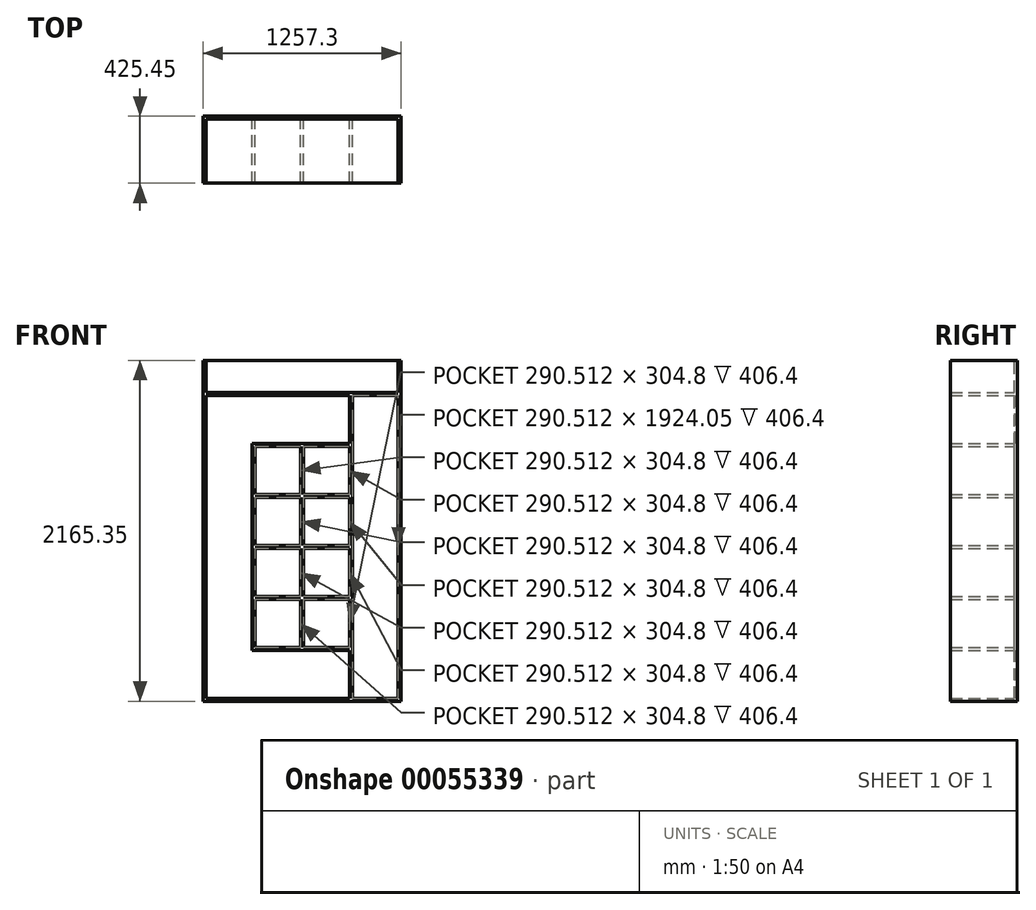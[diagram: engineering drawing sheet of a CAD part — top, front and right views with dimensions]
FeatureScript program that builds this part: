
annotation { "Feature Type Name" : "Feature", "Feature Type Description" : "" }
export const myFeature = defineFeature(function(context is Context, id is Id, definition is map)
    precondition{}
    {
        {
            var Q0;
            Q0=qCreatedBy(makeId("Front.planeOp"),FACE);
            var sketch = newSketch(context, id + "F0", { "sketchPlane" : qUnion([Q0])});
            skLineSegment(sketch, "E0.bottom", {"start": v(-913.34, 1359.41) * mm, "end": v(343.96, 1359.41) * mm});
            skLineSegment(sketch, "E0.top", {"start": v(-913.34, -805.94) * mm, "end": v(343.96, -805.94) * mm});
            skLineSegment(sketch, "E0.left", {"start": v(-913.34, 1359.41) * mm, "end": v(-913.34, -805.94) * mm});
            skLineSegment(sketch, "E0.right", {"start": v(343.96, 1359.41) * mm, "end": v(343.96, -805.94) * mm});
            skSolve(sketch);
        }
        {
            var Q0;
            Q0=makeQuery(id+"F0.imprint","IMPRINT",FACE,{"disambiguationData":[TD([[makeQuery(id+"F0.imprint","IMPRINT",EDGE,{"derivedFrom":sQuery(id+"F0.wireOp",EDGE,"E0.bottom")}),-1.0]])]});
            extrude(context, id + "F1", {"entities" : qUnion([Q0]), "depth" : 19.05 * mm});
        }
        {
            var Q0;
            Q0=makeQuery(id+"F1.opExtrude","CAP_FACE",FACE,{"disambiguationData":[OSD([sQuery(id+"F0.wireOp",EDGE,"E0.bottom"),sQuery(id+"F0.wireOp",EDGE,"E0.top"),sQuery(id+"F0.wireOp",EDGE,"E0.left"),sQuery(id+"F0.wireOp",EDGE,"E0.right")])],"isStart":false});
            var sketch = newSketch(context, id + "F2", { "sketchPlane" : qUnion([Q0])});
            skLineSegment(sketch, "E1.bottom", {"start": v(-913.34, -805.94) * mm, "end": v(-894.3, -805.94) * mm});
            skLineSegment(sketch, "E1.top", {"start": v(-913.34, 1359.41) * mm, "end": v(-894.3, 1359.41) * mm});
            skLineSegment(sketch, "E1.left", {"start": v(-913.34, -805.94) * mm, "end": v(-913.34, 1359.41) * mm});
            skLineSegment(sketch, "E1.right", {"start": v(-894.3, -805.94) * mm, "end": v(-894.3, 1359.41) * mm});
            skLineSegment(sketch, "E2.bottom", {"start": v(343.96, -805.94) * mm, "end": v(324.9, -805.94) * mm});
            skLineSegment(sketch, "E2.top", {"start": v(343.96, 1359.41) * mm, "end": v(324.9, 1359.41) * mm});
            skLineSegment(sketch, "E2.left", {"start": v(343.96, -805.94) * mm, "end": v(343.96, 1359.41) * mm});
            skLineSegment(sketch, "E2.right", {"start": v(324.9, -805.94) * mm, "end": v(324.9, 1359.41) * mm});
            skLineSegment(sketch, "E3.bottom", {"start": v(-894.3, -805.94) * mm, "end": v(324.9, -805.94) * mm});
            skLineSegment(sketch, "E3.top", {"start": v(-894.3, -786.89) * mm, "end": v(324.9, -786.89) * mm});
            skLineSegment(sketch, "E3.left", {"start": v(-894.3, -805.94) * mm, "end": v(-894.3, -786.89) * mm});
            skLineSegment(sketch, "E3.right", {"start": v(324.9, -805.94) * mm, "end": v(324.9, -786.89) * mm});
            skLineSegment(sketch, "E4.bottom", {"start": v(-894.3, -482.09) * mm, "end": v(324.9, -482.09) * mm});
            skLineSegment(sketch, "E4.top", {"start": v(-894.3, -463.04) * mm, "end": v(324.9, -463.04) * mm});
            skLineSegment(sketch, "E4.left", {"start": v(-894.3, -482.09) * mm, "end": v(-894.3, -463.04) * mm});
            skLineSegment(sketch, "E4.right", {"start": v(324.9, -482.09) * mm, "end": v(324.9, -463.04) * mm});
            skLineSegment(sketch, "E5.bottom", {"start": v(-894.3, -158.24) * mm, "end": v(324.9, -158.24) * mm});
            skLineSegment(sketch, "E5.top", {"start": v(-894.3, -139.19) * mm, "end": v(324.9, -139.19) * mm});
            skLineSegment(sketch, "E5.left", {"start": v(-894.3, -158.24) * mm, "end": v(-894.3, -139.19) * mm});
            skLineSegment(sketch, "E5.right", {"start": v(324.9, -158.24) * mm, "end": v(324.9, -139.19) * mm});
            skLineSegment(sketch, "E6.bottom", {"start": v(-894.3, 165.61) * mm, "end": v(324.9, 165.61) * mm});
            skLineSegment(sketch, "E6.top", {"start": v(-894.3, 184.66) * mm, "end": v(324.9, 184.66) * mm});
            skLineSegment(sketch, "E6.left", {"start": v(-894.3, 165.61) * mm, "end": v(-894.3, 184.66) * mm});
            skLineSegment(sketch, "E6.right", {"start": v(324.9, 165.61) * mm, "end": v(324.9, 184.66) * mm});
            skLineSegment(sketch, "E7.bottom", {"start": v(-894.3, 489.46) * mm, "end": v(324.9, 489.46) * mm});
            skLineSegment(sketch, "E7.top", {"start": v(-894.3, 508.51) * mm, "end": v(324.9, 508.51) * mm});
            skLineSegment(sketch, "E7.left", {"start": v(-894.3, 489.46) * mm, "end": v(-894.3, 508.51) * mm});
            skLineSegment(sketch, "E7.right", {"start": v(324.9, 489.46) * mm, "end": v(324.9, 508.51) * mm});
            skLineSegment(sketch, "E8.bottom", {"start": v(-894.3, 813.31) * mm, "end": v(324.9, 813.31) * mm});
            skLineSegment(sketch, "E8.top", {"start": v(-894.3, 832.36) * mm, "end": v(324.9, 832.36) * mm});
            skLineSegment(sketch, "E8.left", {"start": v(-894.3, 813.31) * mm, "end": v(-894.3, 832.36) * mm});
            skLineSegment(sketch, "E8.right", {"start": v(324.9, 813.31) * mm, "end": v(324.9, 832.36) * mm});
            skLineSegment(sketch, "E9.bottom", {"start": v(-894.3, 1137.16) * mm, "end": v(324.9, 1137.16) * mm});
            skLineSegment(sketch, "E9.top", {"start": v(-894.3, 1156.21) * mm, "end": v(324.9, 1156.21) * mm});
            skLineSegment(sketch, "E9.left", {"start": v(-894.3, 1137.16) * mm, "end": v(-894.3, 1156.21) * mm});
            skLineSegment(sketch, "E9.right", {"start": v(324.9, 1137.16) * mm, "end": v(324.9, 1156.21) * mm});
            skLineSegment(sketch, "E10.bottom", {"start": v(-603.78, -786.89) * mm, "end": v(-584.73, -786.89) * mm});
            skLineSegment(sketch, "E10.top", {"start": v(-603.78, 1137.16) * mm, "end": v(-584.73, 1137.16) * mm});
            skLineSegment(sketch, "E10.left", {"start": v(-603.78, -786.89) * mm, "end": v(-603.78, 1137.16) * mm});
            skLineSegment(sketch, "E10.right", {"start": v(-584.73, -786.89) * mm, "end": v(-584.73, 1137.16) * mm});
            skLineSegment(sketch, "E11.bottom", {"start": v(-294.22, -786.89) * mm, "end": v(-275.17, -786.89) * mm});
            skLineSegment(sketch, "E11.top", {"start": v(-294.22, 1137.16) * mm, "end": v(-275.17, 1137.16) * mm});
            skLineSegment(sketch, "E11.left", {"start": v(-294.22, -786.89) * mm, "end": v(-294.22, 1137.16) * mm});
            skLineSegment(sketch, "E11.right", {"start": v(-275.17, -786.89) * mm, "end": v(-275.17, 1137.16) * mm});
            skLineSegment(sketch, "E12.bottom", {"start": v(0, -786.89) * mm, "end": v(19.05, -786.89) * mm});
            skLineSegment(sketch, "E12.top", {"start": v(0, 1137.16) * mm, "end": v(19.05, 1137.16) * mm});
            skLineSegment(sketch, "E13.bottom", {"start": v(34.4, 1137.16) * mm, "end": v(15.35, 1137.16) * mm});
            skLineSegment(sketch, "E13.top", {"start": v(34.4, -786.89) * mm, "end": v(15.35, -786.89) * mm});
            skLineSegment(sketch, "E13.left", {"start": v(34.4, 1137.16) * mm, "end": v(34.4, -786.89) * mm});
            skLineSegment(sketch, "E13.right", {"start": v(15.35, 1137.16) * mm, "end": v(15.35, -786.89) * mm});
            skSolve(sketch);
        }
        {
            var Q0;
            Q0 = qSketchRegion(id + "F2", true);
            var Q1;
            {var subQ0=sQuery(id+"F2.wireOp",EDGE,"E10.left");var subQ1=sQuery(id+"F2.wireOp",EDGE,"E7.top");var subQ2=makeQuery(id+"F2.imprint","INTERSECT",VERTEX,{"derivedFrom":[subQ1,subQ0]});Q1=makeQuery(id+"F2.imprint","IMPRINT",FACE,{"disambiguationData":[TD([[makeQuery(id+"F2.imprint","IMPRINT",EDGE,{"disambiguationData":[TD([[subQ2,-1.0]])],"derivedFrom":subQ1}),1.0]])]});}
            var Q2;
            {var subQ5=sQuery(id+"F2.wireOp",EDGE,"E10.top");Q2=makeQuery(id+"F2.imprint","IMPRINT",FACE,{"disambiguationData":[TD([[makeQuery(id+"F2.imprint","IMPRINT",EDGE,{"derivedFrom":subQ5}),-1.0]])]});}
            var Q3;
            {var subQ0=sQuery(id+"F2.wireOp",EDGE,"E8.left");Q3=makeQuery(id+"F2.imprint","IMPRINT",FACE,{"disambiguationData":[TD([[makeQuery(id+"F2.imprint","IMPRINT",EDGE,{"derivedFrom":subQ0}),-1.0]])]});}
            var Q4;
            {var subQ0=sQuery(id+"F2.wireOp",EDGE,"E10.right");var subQ1=sQuery(id+"F2.wireOp",EDGE,"E8.bottom");var subQ2=makeQuery(id+"F2.imprint","INTERSECT",VERTEX,{"derivedFrom":[subQ1,subQ0]});Q4=makeQuery(id+"F2.imprint","IMPRINT",FACE,{"disambiguationData":[TD([[makeQuery(id+"F2.imprint","IMPRINT",EDGE,{"disambiguationData":[TD([[subQ2,-1.0]])],"derivedFrom":subQ1}),1.0]])]});}
            var Q5;
            {var subQ0=sQuery(id+"F2.wireOp",EDGE,"E10.left");var subQ1=sQuery(id+"F2.wireOp",EDGE,"E8.bottom");var subQ2=makeQuery(id+"F2.imprint","INTERSECT",VERTEX,{"derivedFrom":[subQ1,subQ0]});Q5=makeQuery(id+"F2.imprint","IMPRINT",FACE,{"disambiguationData":[TD([[makeQuery(id+"F2.imprint","IMPRINT",EDGE,{"disambiguationData":[TD([[subQ2,-1.0]])],"derivedFrom":subQ1}),1.0]])]});}
            var Q6;
            {var subQ0=sQuery(id+"F2.wireOp",EDGE,"E11.left");var subQ1=sQuery(id+"F2.wireOp",EDGE,"E8.bottom");var subQ2=makeQuery(id+"F2.imprint","INTERSECT",VERTEX,{"derivedFrom":[subQ1,subQ0]});Q6=makeQuery(id+"F2.imprint","IMPRINT",FACE,{"disambiguationData":[TD([[makeQuery(id+"F2.imprint","IMPRINT",EDGE,{"disambiguationData":[TD([[subQ2,-1.0]])],"derivedFrom":subQ1}),1.0]])]});}
            var Q7;
            {var subQ0=sQuery(id+"F2.wireOp",EDGE,"E11.right");var subQ1=sQuery(id+"F2.wireOp",EDGE,"E8.bottom");var subQ2=makeQuery(id+"F2.imprint","INTERSECT",VERTEX,{"derivedFrom":[subQ1,subQ0]});Q7=makeQuery(id+"F2.imprint","IMPRINT",FACE,{"disambiguationData":[TD([[makeQuery(id+"F2.imprint","IMPRINT",EDGE,{"disambiguationData":[TD([[subQ2,-1.0]])],"derivedFrom":subQ1}),1.0]])]});}
            var Q8;
            {var subQ0=sQuery(id+"F2.wireOp",EDGE,"E13.right");var subQ1=sQuery(id+"F2.wireOp",EDGE,"E8.bottom");var subQ2=makeQuery(id+"F2.imprint","INTERSECT",VERTEX,{"derivedFrom":[subQ1,subQ0]});Q8=makeQuery(id+"F2.imprint","IMPRINT",FACE,{"disambiguationData":[TD([[makeQuery(id+"F2.imprint","IMPRINT",EDGE,{"disambiguationData":[TD([[subQ2,-1.0]])],"derivedFrom":subQ1}),1.0]])]});}
            var Q9;
            {var subQ0=sQuery(id+"F2.wireOp",EDGE,"E8.right");Q9=makeQuery(id+"F2.imprint","IMPRINT",FACE,{"disambiguationData":[TD([[makeQuery(id+"F2.imprint","IMPRINT",EDGE,{"derivedFrom":subQ0}),1.0]])]});}
            var Q10;
            {var subQ3=sQuery(id+"F2.wireOp",EDGE,"E8.top");var subQ5=sQuery(id+"F2.wireOp",EDGE,"E13.right");var subQ8=makeQuery(id+"F2.imprint","INTERSECT",VERTEX,{"derivedFrom":[subQ3,subQ5]});Q10=makeQuery(id+"F2.imprint","IMPRINT",FACE,{"disambiguationData":[TD([[makeQuery(id+"F2.imprint","IMPRINT",EDGE,{"disambiguationData":[TD([[subQ8,-1.0]])],"derivedFrom":subQ3}),1.0]])]});}
            var Q11;
            {var subQ5=sQuery(id+"F2.wireOp",EDGE,"E11.top");Q11=makeQuery(id+"F2.imprint","IMPRINT",FACE,{"disambiguationData":[TD([[makeQuery(id+"F2.imprint","IMPRINT",EDGE,{"derivedFrom":subQ5}),-1.0]])]});}
            var Q12;
            {var subQ0=sQuery(id+"F2.wireOp",EDGE,"E11.left");var subQ1=sQuery(id+"F2.wireOp",EDGE,"E7.top");var subQ2=makeQuery(id+"F2.imprint","INTERSECT",VERTEX,{"derivedFrom":[subQ1,subQ0]});Q12=makeQuery(id+"F2.imprint","IMPRINT",FACE,{"disambiguationData":[TD([[makeQuery(id+"F2.imprint","IMPRINT",EDGE,{"disambiguationData":[TD([[subQ2,-1.0]])],"derivedFrom":subQ1}),1.0]])]});}
            var Q13;
            {var subQ0=sQuery(id+"F2.wireOp",EDGE,"E13.right");var subQ1=sQuery(id+"F2.wireOp",EDGE,"E7.top");var subQ2=makeQuery(id+"F2.imprint","INTERSECT",VERTEX,{"derivedFrom":[subQ1,subQ0]});Q13=makeQuery(id+"F2.imprint","IMPRINT",FACE,{"disambiguationData":[TD([[makeQuery(id+"F2.imprint","IMPRINT",EDGE,{"disambiguationData":[TD([[subQ2,-1.0]])],"derivedFrom":subQ1}),1.0]])]});}
            var Q14;
            {var subQ0=sQuery(id+"F2.wireOp",EDGE,"E7.left");Q14=makeQuery(id+"F2.imprint","IMPRINT",FACE,{"disambiguationData":[TD([[makeQuery(id+"F2.imprint","IMPRINT",EDGE,{"derivedFrom":subQ0}),-1.0]])]});}
            var Q15;
            {var subQ0=sQuery(id+"F2.wireOp",EDGE,"E10.left");var subQ1=sQuery(id+"F2.wireOp",EDGE,"E7.bottom");var subQ2=makeQuery(id+"F2.imprint","INTERSECT",VERTEX,{"derivedFrom":[subQ1,subQ0]});Q15=makeQuery(id+"F2.imprint","IMPRINT",FACE,{"disambiguationData":[TD([[makeQuery(id+"F2.imprint","IMPRINT",EDGE,{"disambiguationData":[TD([[subQ2,-1.0]])],"derivedFrom":subQ1}),1.0]])]});}
            var Q16;
            {var subQ0=sQuery(id+"F2.wireOp",EDGE,"E10.right");var subQ1=sQuery(id+"F2.wireOp",EDGE,"E7.bottom");var subQ2=makeQuery(id+"F2.imprint","INTERSECT",VERTEX,{"derivedFrom":[subQ1,subQ0]});Q16=makeQuery(id+"F2.imprint","IMPRINT",FACE,{"disambiguationData":[TD([[makeQuery(id+"F2.imprint","IMPRINT",EDGE,{"disambiguationData":[TD([[subQ2,-1.0]])],"derivedFrom":subQ1}),1.0]])]});}
            var Q17;
            {var subQ0=sQuery(id+"F2.wireOp",EDGE,"E11.left");var subQ1=sQuery(id+"F2.wireOp",EDGE,"E7.bottom");var subQ2=makeQuery(id+"F2.imprint","INTERSECT",VERTEX,{"derivedFrom":[subQ1,subQ0]});Q17=makeQuery(id+"F2.imprint","IMPRINT",FACE,{"disambiguationData":[TD([[makeQuery(id+"F2.imprint","IMPRINT",EDGE,{"disambiguationData":[TD([[subQ2,-1.0]])],"derivedFrom":subQ1}),1.0]])]});}
            var Q18;
            {var subQ0=sQuery(id+"F2.wireOp",EDGE,"E11.right");var subQ1=sQuery(id+"F2.wireOp",EDGE,"E7.bottom");var subQ2=makeQuery(id+"F2.imprint","INTERSECT",VERTEX,{"derivedFrom":[subQ1,subQ0]});Q18=makeQuery(id+"F2.imprint","IMPRINT",FACE,{"disambiguationData":[TD([[makeQuery(id+"F2.imprint","IMPRINT",EDGE,{"disambiguationData":[TD([[subQ2,-1.0]])],"derivedFrom":subQ1}),1.0]])]});}
            var Q19;
            {var subQ0=sQuery(id+"F2.wireOp",EDGE,"E13.right");var subQ1=sQuery(id+"F2.wireOp",EDGE,"E7.bottom");var subQ2=makeQuery(id+"F2.imprint","INTERSECT",VERTEX,{"derivedFrom":[subQ1,subQ0]});Q19=makeQuery(id+"F2.imprint","IMPRINT",FACE,{"disambiguationData":[TD([[makeQuery(id+"F2.imprint","IMPRINT",EDGE,{"disambiguationData":[TD([[subQ2,-1.0]])],"derivedFrom":subQ1}),1.0]])]});}
            var Q20;
            {var subQ0=sQuery(id+"F2.wireOp",EDGE,"E7.right");Q20=makeQuery(id+"F2.imprint","IMPRINT",FACE,{"disambiguationData":[TD([[makeQuery(id+"F2.imprint","IMPRINT",EDGE,{"derivedFrom":subQ0}),1.0]])]});}
            var Q21;
            {var subQ0=sQuery(id+"F2.wireOp",EDGE,"E6.left");Q21=makeQuery(id+"F2.imprint","IMPRINT",FACE,{"disambiguationData":[TD([[makeQuery(id+"F2.imprint","IMPRINT",EDGE,{"derivedFrom":subQ0}),-1.0]])]});}
            var Q22;
            {var subQ0=sQuery(id+"F2.wireOp",EDGE,"E10.left");var subQ1=sQuery(id+"F2.wireOp",EDGE,"E6.bottom");var subQ2=makeQuery(id+"F2.imprint","INTERSECT",VERTEX,{"derivedFrom":[subQ1,subQ0]});Q22=makeQuery(id+"F2.imprint","IMPRINT",FACE,{"disambiguationData":[TD([[makeQuery(id+"F2.imprint","IMPRINT",EDGE,{"disambiguationData":[TD([[subQ2,-1.0]])],"derivedFrom":subQ1}),1.0]])]});}
            var Q23;
            {var subQ0=sQuery(id+"F2.wireOp",EDGE,"E10.right");var subQ1=sQuery(id+"F2.wireOp",EDGE,"E6.bottom");var subQ2=makeQuery(id+"F2.imprint","INTERSECT",VERTEX,{"derivedFrom":[subQ1,subQ0]});Q23=makeQuery(id+"F2.imprint","IMPRINT",FACE,{"disambiguationData":[TD([[makeQuery(id+"F2.imprint","IMPRINT",EDGE,{"disambiguationData":[TD([[subQ2,-1.0]])],"derivedFrom":subQ1}),1.0]])]});}
            var Q24;
            {var subQ0=sQuery(id+"F2.wireOp",EDGE,"E11.left");var subQ1=sQuery(id+"F2.wireOp",EDGE,"E6.bottom");var subQ2=makeQuery(id+"F2.imprint","INTERSECT",VERTEX,{"derivedFrom":[subQ1,subQ0]});Q24=makeQuery(id+"F2.imprint","IMPRINT",FACE,{"disambiguationData":[TD([[makeQuery(id+"F2.imprint","IMPRINT",EDGE,{"disambiguationData":[TD([[subQ2,-1.0]])],"derivedFrom":subQ1}),1.0]])]});}
            var Q25;
            {var subQ0=sQuery(id+"F2.wireOp",EDGE,"E11.right");var subQ1=sQuery(id+"F2.wireOp",EDGE,"E6.bottom");var subQ2=makeQuery(id+"F2.imprint","INTERSECT",VERTEX,{"derivedFrom":[subQ1,subQ0]});Q25=makeQuery(id+"F2.imprint","IMPRINT",FACE,{"disambiguationData":[TD([[makeQuery(id+"F2.imprint","IMPRINT",EDGE,{"disambiguationData":[TD([[subQ2,-1.0]])],"derivedFrom":subQ1}),1.0]])]});}
            var Q26;
            {var subQ0=sQuery(id+"F2.wireOp",EDGE,"E13.right");var subQ1=sQuery(id+"F2.wireOp",EDGE,"E6.bottom");var subQ2=makeQuery(id+"F2.imprint","INTERSECT",VERTEX,{"derivedFrom":[subQ1,subQ0]});Q26=makeQuery(id+"F2.imprint","IMPRINT",FACE,{"disambiguationData":[TD([[makeQuery(id+"F2.imprint","IMPRINT",EDGE,{"disambiguationData":[TD([[subQ2,-1.0]])],"derivedFrom":subQ1}),1.0]])]});}
            var Q27;
            {var subQ0=sQuery(id+"F2.wireOp",EDGE,"E6.right");Q27=makeQuery(id+"F2.imprint","IMPRINT",FACE,{"disambiguationData":[TD([[makeQuery(id+"F2.imprint","IMPRINT",EDGE,{"derivedFrom":subQ0}),1.0]])]});}
            var Q28;
            {var subQ0=sQuery(id+"F2.wireOp",EDGE,"E13.right");var subQ1=sQuery(id+"F2.wireOp",EDGE,"E6.top");var subQ2=makeQuery(id+"F2.imprint","INTERSECT",VERTEX,{"derivedFrom":[subQ1,subQ0]});Q28=makeQuery(id+"F2.imprint","IMPRINT",FACE,{"disambiguationData":[TD([[makeQuery(id+"F2.imprint","IMPRINT",EDGE,{"disambiguationData":[TD([[subQ2,-1.0]])],"derivedFrom":subQ1}),1.0]])]});}
            var Q29;
            {var subQ0=sQuery(id+"F2.wireOp",EDGE,"E11.left");var subQ1=sQuery(id+"F2.wireOp",EDGE,"E6.top");var subQ2=makeQuery(id+"F2.imprint","INTERSECT",VERTEX,{"derivedFrom":[subQ1,subQ0]});Q29=makeQuery(id+"F2.imprint","IMPRINT",FACE,{"disambiguationData":[TD([[makeQuery(id+"F2.imprint","IMPRINT",EDGE,{"disambiguationData":[TD([[subQ2,-1.0]])],"derivedFrom":subQ1}),1.0]])]});}
            var Q30;
            {var subQ0=sQuery(id+"F2.wireOp",EDGE,"E10.left");var subQ1=sQuery(id+"F2.wireOp",EDGE,"E6.top");var subQ2=makeQuery(id+"F2.imprint","INTERSECT",VERTEX,{"derivedFrom":[subQ1,subQ0]});Q30=makeQuery(id+"F2.imprint","IMPRINT",FACE,{"disambiguationData":[TD([[makeQuery(id+"F2.imprint","IMPRINT",EDGE,{"disambiguationData":[TD([[subQ2,-1.0]])],"derivedFrom":subQ1}),1.0]])]});}
            var Q31;
            {var subQ0=sQuery(id+"F2.wireOp",EDGE,"E5.left");Q31=makeQuery(id+"F2.imprint","IMPRINT",FACE,{"disambiguationData":[TD([[makeQuery(id+"F2.imprint","IMPRINT",EDGE,{"derivedFrom":subQ0}),-1.0]])]});}
            var Q32;
            {var subQ0=sQuery(id+"F2.wireOp",EDGE,"E10.left");var subQ1=sQuery(id+"F2.wireOp",EDGE,"E5.bottom");var subQ2=makeQuery(id+"F2.imprint","INTERSECT",VERTEX,{"derivedFrom":[subQ1,subQ0]});Q32=makeQuery(id+"F2.imprint","IMPRINT",FACE,{"disambiguationData":[TD([[makeQuery(id+"F2.imprint","IMPRINT",EDGE,{"disambiguationData":[TD([[subQ2,-1.0]])],"derivedFrom":subQ1}),1.0]])]});}
            var Q33;
            {var subQ0=sQuery(id+"F2.wireOp",EDGE,"E10.right");var subQ1=sQuery(id+"F2.wireOp",EDGE,"E5.bottom");var subQ2=makeQuery(id+"F2.imprint","INTERSECT",VERTEX,{"derivedFrom":[subQ1,subQ0]});Q33=makeQuery(id+"F2.imprint","IMPRINT",FACE,{"disambiguationData":[TD([[makeQuery(id+"F2.imprint","IMPRINT",EDGE,{"disambiguationData":[TD([[subQ2,-1.0]])],"derivedFrom":subQ1}),1.0]])]});}
            var Q34;
            {var subQ0=sQuery(id+"F2.wireOp",EDGE,"E11.left");var subQ1=sQuery(id+"F2.wireOp",EDGE,"E5.bottom");var subQ2=makeQuery(id+"F2.imprint","INTERSECT",VERTEX,{"derivedFrom":[subQ1,subQ0]});Q34=makeQuery(id+"F2.imprint","IMPRINT",FACE,{"disambiguationData":[TD([[makeQuery(id+"F2.imprint","IMPRINT",EDGE,{"disambiguationData":[TD([[subQ2,-1.0]])],"derivedFrom":subQ1}),1.0]])]});}
            var Q35;
            {var subQ0=sQuery(id+"F2.wireOp",EDGE,"E11.right");var subQ1=sQuery(id+"F2.wireOp",EDGE,"E5.bottom");var subQ2=makeQuery(id+"F2.imprint","INTERSECT",VERTEX,{"derivedFrom":[subQ1,subQ0]});Q35=makeQuery(id+"F2.imprint","IMPRINT",FACE,{"disambiguationData":[TD([[makeQuery(id+"F2.imprint","IMPRINT",EDGE,{"disambiguationData":[TD([[subQ2,-1.0]])],"derivedFrom":subQ1}),1.0]])]});}
            var Q36;
            {var subQ0=sQuery(id+"F2.wireOp",EDGE,"E13.right");var subQ1=sQuery(id+"F2.wireOp",EDGE,"E5.bottom");var subQ2=makeQuery(id+"F2.imprint","INTERSECT",VERTEX,{"derivedFrom":[subQ1,subQ0]});Q36=makeQuery(id+"F2.imprint","IMPRINT",FACE,{"disambiguationData":[TD([[makeQuery(id+"F2.imprint","IMPRINT",EDGE,{"disambiguationData":[TD([[subQ2,-1.0]])],"derivedFrom":subQ1}),1.0]])]});}
            var Q37;
            {var subQ0=sQuery(id+"F2.wireOp",EDGE,"E5.right");Q37=makeQuery(id+"F2.imprint","IMPRINT",FACE,{"disambiguationData":[TD([[makeQuery(id+"F2.imprint","IMPRINT",EDGE,{"derivedFrom":subQ0}),1.0]])]});}
            var Q38;
            {var subQ0=sQuery(id+"F2.wireOp",EDGE,"E10.left");var subQ1=sQuery(id+"F2.wireOp",EDGE,"E5.top");var subQ2=makeQuery(id+"F2.imprint","INTERSECT",VERTEX,{"derivedFrom":[subQ1,subQ0]});Q38=makeQuery(id+"F2.imprint","IMPRINT",FACE,{"disambiguationData":[TD([[makeQuery(id+"F2.imprint","IMPRINT",EDGE,{"disambiguationData":[TD([[subQ2,-1.0]])],"derivedFrom":subQ1}),1.0]])]});}
            var Q39;
            {var subQ0=sQuery(id+"F2.wireOp",EDGE,"E11.left");var subQ1=sQuery(id+"F2.wireOp",EDGE,"E5.top");var subQ2=makeQuery(id+"F2.imprint","INTERSECT",VERTEX,{"derivedFrom":[subQ1,subQ0]});Q39=makeQuery(id+"F2.imprint","IMPRINT",FACE,{"disambiguationData":[TD([[makeQuery(id+"F2.imprint","IMPRINT",EDGE,{"disambiguationData":[TD([[subQ2,-1.0]])],"derivedFrom":subQ1}),1.0]])]});}
            var Q40;
            {var subQ0=sQuery(id+"F2.wireOp",EDGE,"E13.right");var subQ1=sQuery(id+"F2.wireOp",EDGE,"E5.top");var subQ2=makeQuery(id+"F2.imprint","INTERSECT",VERTEX,{"derivedFrom":[subQ1,subQ0]});Q40=makeQuery(id+"F2.imprint","IMPRINT",FACE,{"disambiguationData":[TD([[makeQuery(id+"F2.imprint","IMPRINT",EDGE,{"disambiguationData":[TD([[subQ2,-1.0]])],"derivedFrom":subQ1}),1.0]])]});}
            var Q41;
            {var subQ0=sQuery(id+"F2.wireOp",EDGE,"E4.left");Q41=makeQuery(id+"F2.imprint","IMPRINT",FACE,{"disambiguationData":[TD([[makeQuery(id+"F2.imprint","IMPRINT",EDGE,{"derivedFrom":subQ0}),-1.0]])]});}
            var Q42;
            {var subQ0=sQuery(id+"F2.wireOp",EDGE,"E10.left");var subQ1=sQuery(id+"F2.wireOp",EDGE,"E4.bottom");var subQ2=makeQuery(id+"F2.imprint","INTERSECT",VERTEX,{"derivedFrom":[subQ1,subQ0]});Q42=makeQuery(id+"F2.imprint","IMPRINT",FACE,{"disambiguationData":[TD([[makeQuery(id+"F2.imprint","IMPRINT",EDGE,{"disambiguationData":[TD([[subQ2,-1.0]])],"derivedFrom":subQ1}),1.0]])]});}
            var Q43;
            {var subQ0=sQuery(id+"F2.wireOp",EDGE,"E10.right");var subQ1=sQuery(id+"F2.wireOp",EDGE,"E4.bottom");var subQ2=makeQuery(id+"F2.imprint","INTERSECT",VERTEX,{"derivedFrom":[subQ1,subQ0]});Q43=makeQuery(id+"F2.imprint","IMPRINT",FACE,{"disambiguationData":[TD([[makeQuery(id+"F2.imprint","IMPRINT",EDGE,{"disambiguationData":[TD([[subQ2,-1.0]])],"derivedFrom":subQ1}),1.0]])]});}
            var Q44;
            {var subQ0=sQuery(id+"F2.wireOp",EDGE,"E11.left");var subQ1=sQuery(id+"F2.wireOp",EDGE,"E4.bottom");var subQ2=makeQuery(id+"F2.imprint","INTERSECT",VERTEX,{"derivedFrom":[subQ1,subQ0]});Q44=makeQuery(id+"F2.imprint","IMPRINT",FACE,{"disambiguationData":[TD([[makeQuery(id+"F2.imprint","IMPRINT",EDGE,{"disambiguationData":[TD([[subQ2,-1.0]])],"derivedFrom":subQ1}),1.0]])]});}
            var Q45;
            {var subQ0=sQuery(id+"F2.wireOp",EDGE,"E11.right");var subQ1=sQuery(id+"F2.wireOp",EDGE,"E4.bottom");var subQ2=makeQuery(id+"F2.imprint","INTERSECT",VERTEX,{"derivedFrom":[subQ1,subQ0]});Q45=makeQuery(id+"F2.imprint","IMPRINT",FACE,{"disambiguationData":[TD([[makeQuery(id+"F2.imprint","IMPRINT",EDGE,{"disambiguationData":[TD([[subQ2,-1.0]])],"derivedFrom":subQ1}),1.0]])]});}
            var Q46;
            {var subQ0=sQuery(id+"F2.wireOp",EDGE,"E13.right");var subQ1=sQuery(id+"F2.wireOp",EDGE,"E4.bottom");var subQ2=makeQuery(id+"F2.imprint","INTERSECT",VERTEX,{"derivedFrom":[subQ1,subQ0]});Q46=makeQuery(id+"F2.imprint","IMPRINT",FACE,{"disambiguationData":[TD([[makeQuery(id+"F2.imprint","IMPRINT",EDGE,{"disambiguationData":[TD([[subQ2,-1.0]])],"derivedFrom":subQ1}),1.0]])]});}
            var Q47;
            {var subQ0=sQuery(id+"F2.wireOp",EDGE,"E4.right");Q47=makeQuery(id+"F2.imprint","IMPRINT",FACE,{"disambiguationData":[TD([[makeQuery(id+"F2.imprint","IMPRINT",EDGE,{"derivedFrom":subQ0}),1.0]])]});}
            var Q48;
            {var subQ0=sQuery(id+"F2.wireOp",EDGE,"E10.left");var subQ1=sQuery(id+"F2.wireOp",EDGE,"E4.top");var subQ2=makeQuery(id+"F2.imprint","INTERSECT",VERTEX,{"derivedFrom":[subQ1,subQ0]});Q48=makeQuery(id+"F2.imprint","IMPRINT",FACE,{"disambiguationData":[TD([[makeQuery(id+"F2.imprint","IMPRINT",EDGE,{"disambiguationData":[TD([[subQ2,-1.0]])],"derivedFrom":subQ1}),1.0]])]});}
            var Q49;
            {var subQ0=sQuery(id+"F2.wireOp",EDGE,"E11.left");var subQ1=sQuery(id+"F2.wireOp",EDGE,"E4.top");var subQ2=makeQuery(id+"F2.imprint","INTERSECT",VERTEX,{"derivedFrom":[subQ1,subQ0]});Q49=makeQuery(id+"F2.imprint","IMPRINT",FACE,{"disambiguationData":[TD([[makeQuery(id+"F2.imprint","IMPRINT",EDGE,{"disambiguationData":[TD([[subQ2,-1.0]])],"derivedFrom":subQ1}),1.0]])]});}
            var Q50;
            {var subQ0=sQuery(id+"F2.wireOp",EDGE,"E13.right");var subQ1=sQuery(id+"F2.wireOp",EDGE,"E4.top");var subQ2=makeQuery(id+"F2.imprint","INTERSECT",VERTEX,{"derivedFrom":[subQ1,subQ0]});Q50=makeQuery(id+"F2.imprint","IMPRINT",FACE,{"disambiguationData":[TD([[makeQuery(id+"F2.imprint","IMPRINT",EDGE,{"disambiguationData":[TD([[subQ2,-1.0]])],"derivedFrom":subQ1}),1.0]])]});}
            var Q51;
            {var subQ3=sQuery(id+"F2.wireOp",EDGE,"E4.bottom");var subQ5=sQuery(id+"F2.wireOp",EDGE,"E13.right");var subQ8=makeQuery(id+"F2.imprint","INTERSECT",VERTEX,{"derivedFrom":[subQ3,subQ5]});Q51=makeQuery(id+"F2.imprint","IMPRINT",FACE,{"disambiguationData":[TD([[makeQuery(id+"F2.imprint","IMPRINT",EDGE,{"disambiguationData":[TD([[subQ8,-1.0]])],"derivedFrom":subQ3}),-1.0]])]});}
            var Q52;
            {var subQ5=sQuery(id+"F2.wireOp",EDGE,"E11.bottom");Q52=makeQuery(id+"F2.imprint","IMPRINT",FACE,{"disambiguationData":[TD([[makeQuery(id+"F2.imprint","IMPRINT",EDGE,{"derivedFrom":subQ5}),1.0]])]});}
            var Q53;
            {var subQ5=sQuery(id+"F2.wireOp",EDGE,"E10.bottom");Q53=makeQuery(id+"F2.imprint","IMPRINT",FACE,{"disambiguationData":[TD([[makeQuery(id+"F2.imprint","IMPRINT",EDGE,{"derivedFrom":subQ5}),1.0]])]});}
            extrude(context, id + "F3", {"entities" : qUnion([Q0, Q1, Q2, Q3, Q4, Q5, Q6, Q7, Q8, Q9, Q10, Q11, Q12, Q13, Q14, Q15, Q16, Q17, Q18, Q19, Q20, Q21, Q22, Q23, Q24, Q25, Q26, Q27, Q28, Q29, Q30, Q31, Q32, Q33, Q34, Q35, Q36, Q37, Q38, Q39, Q40, Q41, Q42, Q43, Q44, Q45, Q46, Q47, Q48, Q49, Q50, Q51, Q52, Q53]), "operationType" : NewBodyOperationType.ADD, "depth" : 406.4 * mm});
        }
    });
